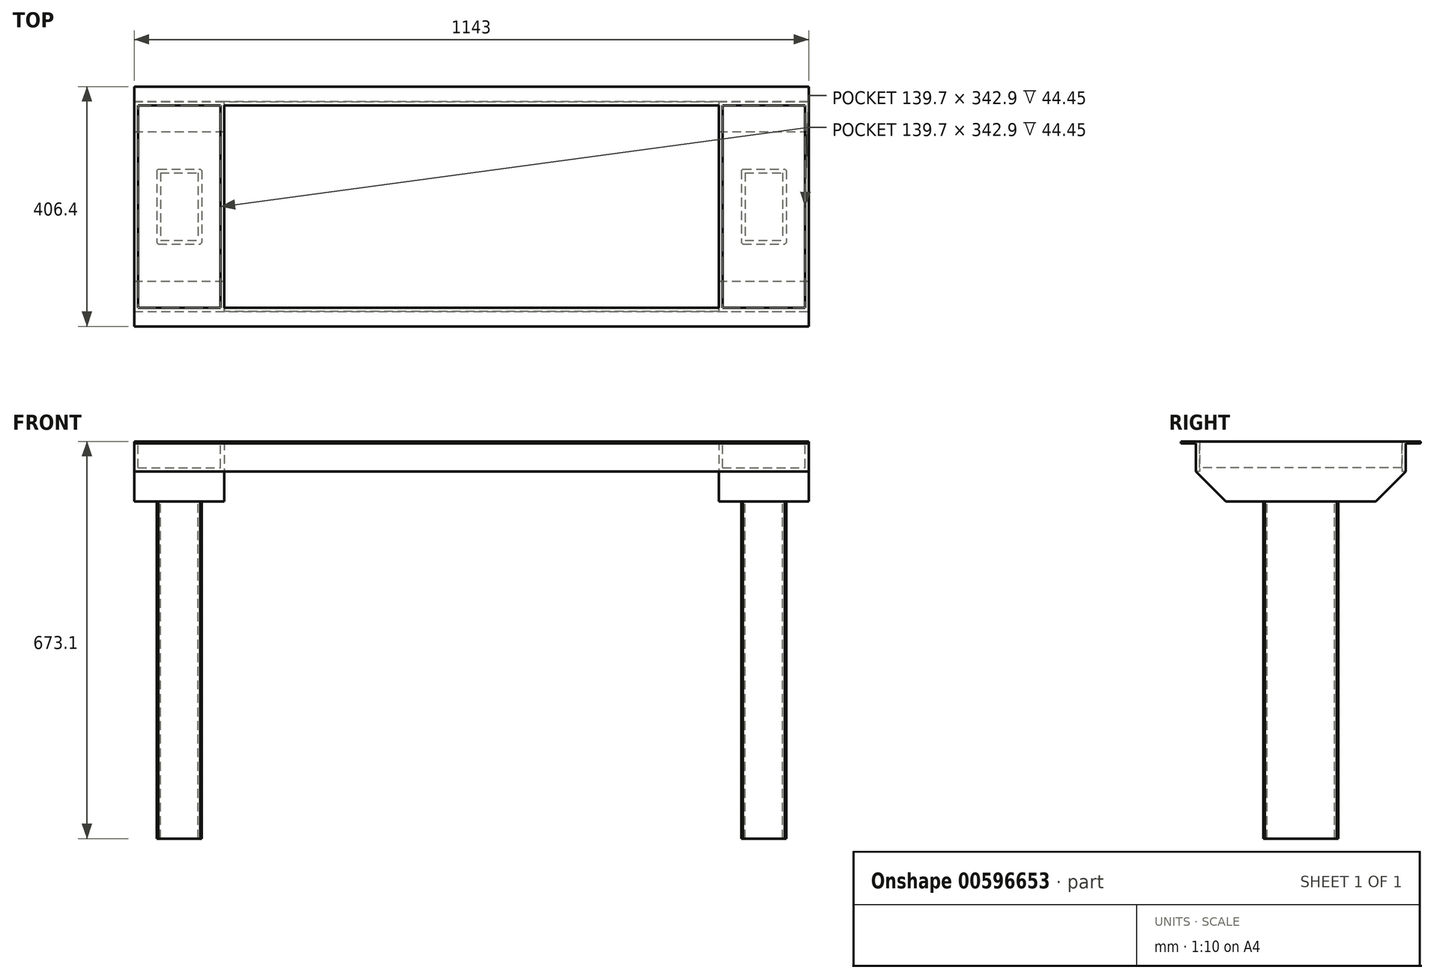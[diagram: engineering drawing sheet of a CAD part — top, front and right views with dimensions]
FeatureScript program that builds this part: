
annotation { "Feature Type Name" : "Feature", "Feature Type Description" : "" }
export const myFeature = defineFeature(function(context is Context, id is Id, definition is map)
    precondition{}
    {
        {
            var Q0;
            Q0=qCreatedBy(makeId("Top.planeOp"),FACE);
            var sketch = newSketch(context, id + "F0", { "sketchPlane" : qUnion([Q0])});
            skLineSegment(sketch, "E0.bottom", {"start": v(571.5, 177.8) * mm, "end": v(-571.5, 177.8) * mm});
            skLineSegment(sketch, "E0.top", {"start": v(571.5, -177.8) * mm, "end": v(-571.5, -177.8) * mm});
            skLineSegment(sketch, "E0.left", {"start": v(571.5, 177.8) * mm, "end": v(571.5, -177.8) * mm});
            skLineSegment(sketch, "E0.right", {"start": v(-571.5, 177.8) * mm, "end": v(-571.5, -177.8) * mm});
            skPoint(sketch, "E0.middle", {"position": v(0, 0) * mm});
            skLineSegment(sketch, "E1.bottom", {"start": v(419.1, 171.45) * mm, "end": v(-419.1, 171.45) * mm});
            skLineSegment(sketch, "E1.top", {"start": v(419.1, -171.45) * mm, "end": v(-419.1, -171.45) * mm});
            skLineSegment(sketch, "E1.left", {"start": v(419.1, 171.45) * mm, "end": v(419.1, -171.45) * mm});
            skLineSegment(sketch, "E1.right", {"start": v(-419.1, 171.45) * mm, "end": v(-419.1, -171.45) * mm});
            skSolve(sketch);
        }
        {
            var Q0;
            Q0=makeQuery(id+"F0.imprint","IMPRINT",FACE,{"disambiguationData":[TD([[makeQuery(id+"F0.imprint","IMPRINT",EDGE,{"derivedFrom":sQuery(id+"F0.wireOp",EDGE,"E0.bottom")}),1.0]])]});
            extrude(context, id + "F1", {"entities" : qUnion([Q0]), "depth" : 50.8 * mm, "offsetDistance" : 25.4 * mm});
        }
        {
            var Q0;
            Q0=makeQuery(id+"F1.opExtrude","CAP_FACE",FACE,{"disambiguationData":[OSD([sQuery(id+"F0.wireOp",EDGE,"E0.bottom"),sQuery(id+"F0.wireOp",EDGE,"E0.top"),sQuery(id+"F0.wireOp",EDGE,"E0.left"),sQuery(id+"F0.wireOp",EDGE,"E0.right"),sQuery(id+"F0.wireOp",EDGE,"E1.bottom"),sQuery(id+"F0.wireOp",EDGE,"E1.top"),sQuery(id+"F0.wireOp",EDGE,"E1.left"),sQuery(id+"F0.wireOp",EDGE,"E1.right")])],"isStart":false});
            var sketch = newSketch(context, id + "F2", { "sketchPlane" : qUnion([Q0])});
            skLineSegment(sketch, "E2", {"start": v(-571.5, 177.8) * mm, "end": v(-571.5, 171.45) * mm});
            skLineSegment(sketch, "E3", {"start": v(-571.5, 171.45) * mm, "end": v(-565.15, 171.45) * mm});
            skLineSegment(sketch, "E4", {"start": v(-419.1, -171.45) * mm, "end": v(-425.45, -171.45) * mm});
            skLineSegment(sketch, "E5.bottom", {"start": v(-565.15, 171.45) * mm, "end": v(-425.45, 171.45) * mm});
            skLineSegment(sketch, "E5.top", {"start": v(-565.15, -171.45) * mm, "end": v(-425.45, -171.45) * mm});
            skLineSegment(sketch, "E5.left", {"start": v(-565.15, 171.45) * mm, "end": v(-565.15, -171.45) * mm});
            skLineSegment(sketch, "E5.right", {"start": v(-425.45, 171.45) * mm, "end": v(-425.45, -171.45) * mm});
            skLineSegment(sketch, "E6", {"start": v(419.1, 171.45) * mm, "end": v(425.45, 171.45) * mm});
            skLineSegment(sketch, "E7", {"start": v(571.5, -177.8) * mm, "end": v(571.5, -171.45) * mm});
            skLineSegment(sketch, "E8", {"start": v(571.5, -171.45) * mm, "end": v(565.15, -171.45) * mm});
            skLineSegment(sketch, "E9.bottom", {"start": v(425.45, 171.45) * mm, "end": v(565.15, 171.45) * mm});
            skLineSegment(sketch, "E9.top", {"start": v(425.45, -171.45) * mm, "end": v(565.15, -171.45) * mm});
            skLineSegment(sketch, "E9.left", {"start": v(425.45, 171.45) * mm, "end": v(425.45, -171.45) * mm});
            skLineSegment(sketch, "E9.right", {"start": v(565.15, 171.45) * mm, "end": v(565.15, -171.45) * mm});
            skSolve(sketch);
        }
        {
            var Q0;
            Q0=makeQuery(id+"F2.imprint","IMPRINT",FACE,{"disambiguationData":[TD([[makeQuery(id+"F2.imprint","IMPRINT",EDGE,{"derivedFrom":sQuery(id+"F2.wireOp",EDGE,"E5.bottom")}),-1.0]])]});
            var Q1;
            Q1=makeQuery(id+"F2.imprint","IMPRINT",FACE,{"disambiguationData":[TD([[makeQuery(id+"F2.imprint","IMPRINT",EDGE,{"derivedFrom":sQuery(id+"F2.wireOp",EDGE,"E9.bottom")}),-1.0]])]});
            extrude(context, id + "F3", {"entities" : qUnion([Q0, Q1]), "operationType" : NewBodyOperationType.REMOVE, "oppositeDirection" : true, "depth" : 44.45 * mm, "offsetDistance" : 25.4 * mm});
        }
        {
            var Q0;
            Q0=makeQuery(id+"F1.opExtrude","SWEPT_FACE",FACE,{"disambiguationData":[OSD([sQuery(id+"F0.wireOp",EDGE,"E0.top")])]});
            var sketch = newSketch(context, id + "F4", { "sketchPlane" : qUnion([Q0])});
            skLineSegment(sketch, "E10.bottom", {"start": v(-571.5, 50.8) * mm, "end": v(571.5, 50.8) * mm});
            skLineSegment(sketch, "E10.top", {"start": v(-571.5, 47.63) * mm, "end": v(571.5, 47.63) * mm});
            skLineSegment(sketch, "E10.left", {"start": v(-571.5, 50.8) * mm, "end": v(-571.5, 47.63) * mm});
            skLineSegment(sketch, "E10.right", {"start": v(571.5, 50.8) * mm, "end": v(571.5, 47.63) * mm});
            skSolve(sketch);
        }
        {
            var Q0;
            Q0=makeQuery(id+"F4.imprint","IMPRINT",FACE,{"disambiguationData":[TD([[makeQuery(id+"F4.imprint","IMPRINT",EDGE,{"derivedFrom":sQuery(id+"F4.wireOp",EDGE,"E10.bottom")}),1.0]])]});
            extrude(context, id + "F5", {"entities" : qUnion([Q0]), "operationType" : NewBodyOperationType.ADD, "depth" : 25.4 * mm, "offsetDistance" : 25.4 * mm});
        }
        {
            var Q0;
            Q0=makeQuery(id+"F1.opExtrude","SWEPT_FACE",FACE,{"disambiguationData":[OSD([sQuery(id+"F0.wireOp",EDGE,"E0.bottom")])]});
            var sketch = newSketch(context, id + "F6", { "sketchPlane" : qUnion([Q0])});
            skLineSegment(sketch, "E11.bottom", {"start": v(571.5, 50.8) * mm, "end": v(-571.5, 50.8) * mm});
            skLineSegment(sketch, "E11.top", {"start": v(571.5, 47.63) * mm, "end": v(-571.5, 47.62) * mm});
            skLineSegment(sketch, "E11.left", {"start": v(571.5, 50.8) * mm, "end": v(571.5, 47.63) * mm});
            skLineSegment(sketch, "E11.right", {"start": v(-571.5, 50.8) * mm, "end": v(-571.5, 47.62) * mm});
            skSolve(sketch);
        }
        {
            var Q0;
            Q0=makeQuery(id+"F6.imprint","IMPRINT",FACE,{"disambiguationData":[TD([[makeQuery(id+"F6.imprint","IMPRINT",EDGE,{"derivedFrom":sQuery(id+"F6.wireOp",EDGE,"E11.bottom")}),-1.0]])]});
            extrude(context, id + "F7", {"entities" : qUnion([Q0]), "operationType" : NewBodyOperationType.ADD, "depth" : 25.4 * mm, "offsetDistance" : 25.4 * mm});
        }
        {
            var Q0;
            Q0=makeQuery(id+"F1.opExtrude","CAP_FACE",FACE,{"disambiguationData":[OSD([sQuery(id+"F0.wireOp",EDGE,"E0.bottom"),sQuery(id+"F0.wireOp",EDGE,"E0.top"),sQuery(id+"F0.wireOp",EDGE,"E0.left"),sQuery(id+"F0.wireOp",EDGE,"E0.right"),sQuery(id+"F0.wireOp",EDGE,"E1.bottom"),sQuery(id+"F0.wireOp",EDGE,"E1.top"),sQuery(id+"F0.wireOp",EDGE,"E1.left"),sQuery(id+"F0.wireOp",EDGE,"E1.right")])],"isStart":true});
            var sketch = newSketch(context, id + "F8", { "sketchPlane" : qUnion([Q0])});
            skLineSegment(sketch, "E12.bottom", {"start": v(-571.5, 177.8) * mm, "end": v(-419.1, 177.8) * mm});
            skLineSegment(sketch, "E12.top", {"start": v(-571.5, -177.8) * mm, "end": v(-419.1, -177.8) * mm});
            skLineSegment(sketch, "E12.left", {"start": v(-571.5, 177.8) * mm, "end": v(-571.5, -177.8) * mm});
            skLineSegment(sketch, "E12.right", {"start": v(-419.1, 177.8) * mm, "end": v(-419.1, -177.8) * mm});
            skLineSegment(sketch, "E13.bottom", {"start": v(571.5, -177.8) * mm, "end": v(419.1, -177.8) * mm});
            skLineSegment(sketch, "E13.top", {"start": v(571.5, 177.8) * mm, "end": v(419.1, 177.8) * mm});
            skLineSegment(sketch, "E13.left", {"start": v(571.5, -177.8) * mm, "end": v(571.5, 177.8) * mm});
            skLineSegment(sketch, "E13.right", {"start": v(419.1, -177.8) * mm, "end": v(419.1, 177.8) * mm});
            skSolve(sketch);
        }
        {
            var Q0;
            {var subQ4=sQuery(id+"F8.wireOp",EDGE,"E12.bottom");Q0=makeQuery(id+"F8.imprint","IMPRINT",FACE,{"disambiguationData":[TD([[makeQuery(id+"F8.imprint","IMPRINT",EDGE,{"derivedFrom":subQ4}),1.0]])]});}
            var Q1;
            {var subQ4=sQuery(id+"F8.wireOp",EDGE,"E13.bottom");Q1=makeQuery(id+"F8.imprint","IMPRINT",FACE,{"disambiguationData":[TD([[makeQuery(id+"F8.imprint","IMPRINT",EDGE,{"derivedFrom":subQ4}),-1.0]])]});}
            extrude(context, id + "F9", {"entities" : qUnion([Q0, Q1]), "operationType" : NewBodyOperationType.ADD, "depth" : 50.8 * mm, "offsetDistance" : 25.4 * mm});
        }
        {
            var Q0;
            Q0=makeQuery(id+"F9.opExtrude","CAP_EDGE",EDGE,{"disambiguationData":[OSD([sQuery(id+"F8.wireOp",EDGE,"E12.top")])],"isStart":false});
            var Q1;
            Q1=makeQuery(id+"F9.opExtrude","CAP_EDGE",EDGE,{"disambiguationData":[OSD([sQuery(id+"F8.wireOp",EDGE,"E12.bottom")])],"isStart":false});
            var Q2;
            Q2=makeQuery(id+"F9.opExtrude","CAP_EDGE",EDGE,{"disambiguationData":[OSD([sQuery(id+"F8.wireOp",EDGE,"E13.top")])],"isStart":false});
            var Q3;
            Q3=makeQuery(id+"F9.opExtrude","CAP_EDGE",EDGE,{"disambiguationData":[OSD([sQuery(id+"F8.wireOp",EDGE,"E13.bottom")])],"isStart":false});
            chamfer(context, id + "F10", {"entities" : qUnion([Q0, Q1, Q2, Q3]), "width" : 50.8 * mm, "tangentPropagation" : true});
        }
        {
            var Q0;
            Q0=makeQuery(id+"F9.opExtrude","CAP_FACE",FACE,{"disambiguationData":[OSD([sQuery(id+"F8.wireOp",EDGE,"E13.bottom"),sQuery(id+"F8.wireOp",EDGE,"E13.top"),sQuery(id+"F8.wireOp",EDGE,"E13.left"),sQuery(id+"F8.wireOp",EDGE,"E13.right")])],"isStart":false});
            var sketch = newSketch(context, id + "F11", { "sketchPlane" : qUnion([Q0])});
            skLineSegment(sketch, "E14", {"start": v(495.3, -127) * mm, "end": v(495.3, 0) * mm});
            skPoint(sketch, "E14.endSnap0", {"position": v(419.1, 0) * mm});
            skLineSegment(sketch, "E15.bottom", {"start": v(457.2, -63.5) * mm, "end": v(533.4, -63.5) * mm});
            skLineSegment(sketch, "E15.top", {"start": v(457.2, 63.5) * mm, "end": v(533.4, 63.5) * mm});
            skLineSegment(sketch, "E15.left", {"start": v(457.2, -63.5) * mm, "end": v(457.2, 63.5) * mm});
            skLineSegment(sketch, "E15.right", {"start": v(533.4, -63.5) * mm, "end": v(533.4, 63.5) * mm});
            skPoint(sketch, "E15.middle", {"position": v(495.3, 0) * mm});
            skPoint(sketch, "E15.cornerSnap0", {"position": v(495.3, -63.5) * mm});
            skLineSegment(sketch, "E16.bottom", {"start": v(463.55, -57.15) * mm, "end": v(527.05, -57.15) * mm});
            skLineSegment(sketch, "E16.top", {"start": v(463.55, 57.15) * mm, "end": v(527.05, 57.15) * mm});
            skLineSegment(sketch, "E16.left", {"start": v(463.55, -57.15) * mm, "end": v(463.55, 57.15) * mm});
            skLineSegment(sketch, "E16.right", {"start": v(527.05, -57.15) * mm, "end": v(527.05, 57.15) * mm});
            skSolve(sketch);
        }
        {
            var Q0;
            Q0=makeQuery(id+"F9.opExtrude","CAP_FACE",FACE,{"disambiguationData":[OSD([sQuery(id+"F8.wireOp",EDGE,"E12.bottom"),sQuery(id+"F8.wireOp",EDGE,"E12.top"),sQuery(id+"F8.wireOp",EDGE,"E12.left"),sQuery(id+"F8.wireOp",EDGE,"E12.right")])],"isStart":false});
            var sketch = newSketch(context, id + "F12", { "sketchPlane" : qUnion([Q0])});
            skLineSegment(sketch, "E17", {"start": v(-495.3, -127) * mm, "end": v(-495.3, 0) * mm});
            skPoint(sketch, "E17.endSnap0", {"position": v(-419.1, 0) * mm});
            skLineSegment(sketch, "E18.bottom", {"start": v(-533.4, -63.5) * mm, "end": v(-457.2, -63.5) * mm});
            skLineSegment(sketch, "E18.top", {"start": v(-533.4, 63.5) * mm, "end": v(-457.2, 63.5) * mm});
            skLineSegment(sketch, "E18.left", {"start": v(-533.4, -63.5) * mm, "end": v(-533.4, 63.5) * mm});
            skLineSegment(sketch, "E18.right", {"start": v(-457.2, -63.5) * mm, "end": v(-457.2, 63.5) * mm});
            skPoint(sketch, "E18.middle", {"position": v(-495.3, 0) * mm});
            skLineSegment(sketch, "E19.bottom", {"start": v(-527.05, -57.15) * mm, "end": v(-463.55, -57.15) * mm});
            skLineSegment(sketch, "E19.top", {"start": v(-527.05, 57.15) * mm, "end": v(-463.55, 57.15) * mm});
            skLineSegment(sketch, "E19.left", {"start": v(-527.05, -57.15) * mm, "end": v(-527.05, 57.15) * mm});
            skLineSegment(sketch, "E19.right", {"start": v(-463.55, -57.15) * mm, "end": v(-463.55, 57.15) * mm});
            skSolve(sketch);
        }
        {
            var Q0;
            Q0=makeQuery(id+"F11.imprint","IMPRINT",FACE,{"disambiguationData":[TD([[makeQuery(id+"F11.imprint","IMPRINT",EDGE,{"derivedFrom":sQuery(id+"F11.wireOp",EDGE,"E15.top")}),-1.0]])]});
            var Q1;
            Q1=makeQuery(id+"F12.imprint","IMPRINT",FACE,{"disambiguationData":[TD([[makeQuery(id+"F12.imprint","IMPRINT",EDGE,{"derivedFrom":sQuery(id+"F12.wireOp",EDGE,"E18.top")}),-1.0]])]});
            extrude(context, id + "F13", {"entities" : qUnion([Q0, Q1]), "operationType" : NewBodyOperationType.ADD, "depth" : 571.5 * mm, "offsetDistance" : 25.4 * mm});
        }
        {
            var Q0;
            Q0=makeQuery(id+"F13.opExtrude","SWEPT_EDGE",EDGE,{"disambiguationData":[OSD([sQuery(id+"F12.wireOp",EDGE,"E18.top"),sQuery(id+"F12.wireOp",EDGE,"E18.right")])]});
            var Q1;
            Q1=makeQuery(id+"F13.opExtrude","SWEPT_EDGE",EDGE,{"disambiguationData":[OSD([sQuery(id+"F12.wireOp",EDGE,"E18.top"),sQuery(id+"F12.wireOp",EDGE,"E18.left")])]});
            var Q2;
            Q2=makeQuery(id+"F13.opExtrude","SWEPT_EDGE",EDGE,{"disambiguationData":[OSD([sQuery(id+"F12.wireOp",EDGE,"E18.bottom"),sQuery(id+"F12.wireOp",EDGE,"E18.right")])]});
            var Q3;
            Q3=makeQuery(id+"F13.opExtrude","SWEPT_EDGE",EDGE,{"disambiguationData":[OSD([sQuery(id+"F11.wireOp",EDGE,"E15.top"),sQuery(id+"F11.wireOp",EDGE,"E15.right")])]});
            var Q4;
            Q4=makeQuery(id+"F13.opExtrude","SWEPT_EDGE",EDGE,{"disambiguationData":[OSD([sQuery(id+"F11.wireOp",EDGE,"E15.top"),sQuery(id+"F11.wireOp",EDGE,"E15.left")])]});
            var Q5;
            Q5=makeQuery(id+"F13.opExtrude","SWEPT_EDGE",EDGE,{"disambiguationData":[OSD([sQuery(id+"F11.wireOp",EDGE,"E15.bottom"),sQuery(id+"F11.wireOp",EDGE,"E15.right")])]});
            var Q6;
            Q6=makeQuery(id+"F13.opExtrude","SWEPT_EDGE",EDGE,{"disambiguationData":[OSD([sQuery(id+"F11.wireOp",EDGE,"E15.bottom"),sQuery(id+"F11.wireOp",EDGE,"E15.left")])]});
            var Q7;
            Q7=makeQuery(id+"F13.opExtrude","SWEPT_EDGE",EDGE,{"disambiguationData":[OSD([sQuery(id+"F12.wireOp",EDGE,"E18.bottom"),sQuery(id+"F12.wireOp",EDGE,"E18.left")])]});
            chamfer(context, id + "F14", {"entities" : qUnion([Q0, Q1, Q2, Q3, Q4, Q5, Q6, Q7]), "width" : 2.54 * mm, "tangentPropagation" : true});
        }
    });
